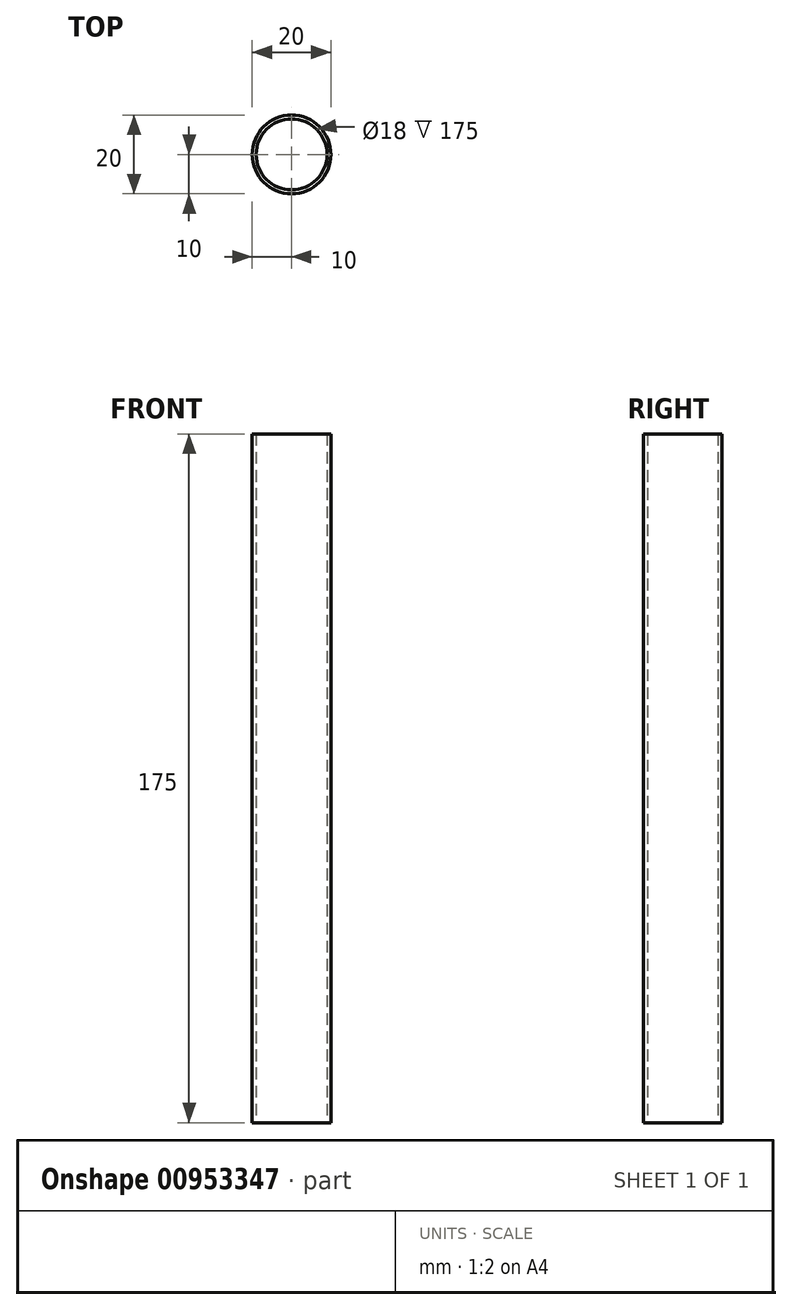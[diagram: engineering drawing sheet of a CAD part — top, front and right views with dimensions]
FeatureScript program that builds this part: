
annotation { "Feature Type Name" : "Feature", "Feature Type Description" : "" }
export const myFeature = defineFeature(function(context is Context, id is Id, definition is map)
    precondition{}
    {
        {
            var Q0;
            Q0=qCreatedBy(makeId("Top.planeOp"),FACE);
            var sketch = newSketch(context, id + "F0", { "sketchPlane" : qUnion([Q0])});
            skCircle(sketch, "E0", {"center": v(0, 0) * mm, "radius": 10 * mm});
            skCircle(sketch, "E1.0", {"center": v(0, 0) * mm, "radius": 9 * mm});
            skSolve(sketch);
        }
        {
            var Q0;
            Q0=makeQuery(id+"F0.imprint","IMPRINT",FACE,{"disambiguationData":[TD([[makeQuery(id+"F0.imprint","IMPRINT",EDGE,{"derivedFrom":sQuery(id+"F0.wireOp",EDGE,"E0")}),1.0]])]});
            extrude(context, id + "F1", {"entities" : qUnion([Q0]), "endBound" : BoundingType.SYMMETRIC, "depth" : 175 * mm, "offsetDistance" : 25 * mm});
        }
    });
